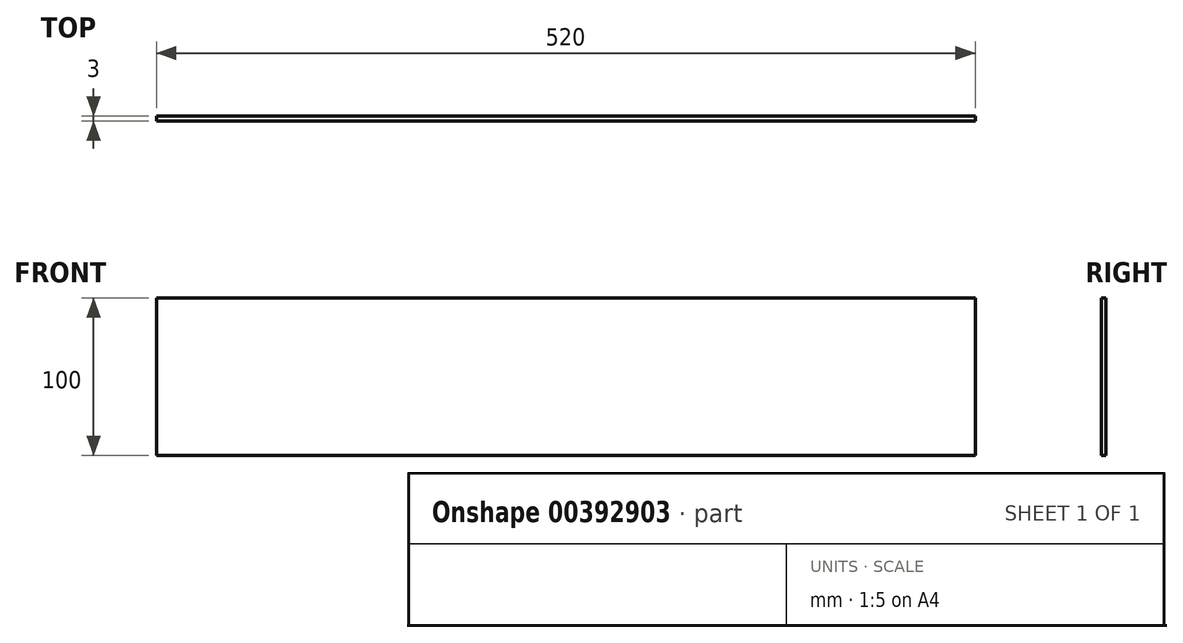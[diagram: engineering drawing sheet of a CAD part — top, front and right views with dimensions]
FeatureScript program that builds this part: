
annotation { "Feature Type Name" : "Feature", "Feature Type Description" : "" }
export const myFeature = defineFeature(function(context is Context, id is Id, definition is map)
    precondition{}
    {
        {
            var Q0;
            Q0=qCreatedBy(makeId("Front.planeOp"),FACE);
            var sketch = newSketch(context, id + "F0", { "sketchPlane" : qUnion([Q0])});
            skLineSegment(sketch, "E0.bottom", {"start": v(0, 0) * mm, "end": v(520, 0) * mm});
            skLineSegment(sketch, "E0.top", {"start": v(0, 100) * mm, "end": v(520, 100) * mm});
            skLineSegment(sketch, "E0.left", {"start": v(0, 0) * mm, "end": v(0, 100) * mm});
            skLineSegment(sketch, "E0.right", {"start": v(520, 0) * mm, "end": v(520, 100) * mm});
            skSolve(sketch);
        }
        {
            var Q0;
            Q0 = qSketchRegion(id + "F0", true);
            extrude(context, id + "F1", {"entities" : qUnion([Q0]), "oppositeDirection" : true, "depth" : 3 * mm});
        }
    });
